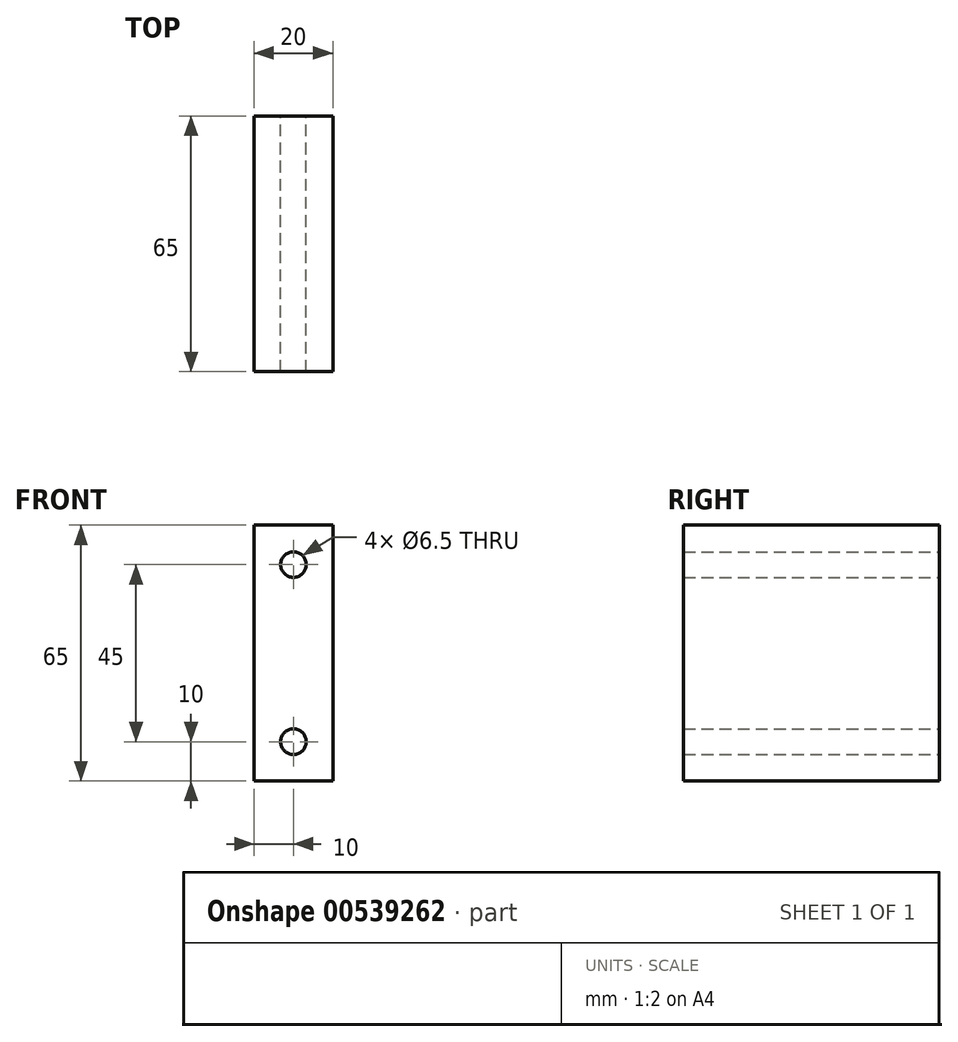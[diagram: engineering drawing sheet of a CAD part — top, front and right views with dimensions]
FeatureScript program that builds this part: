
annotation { "Feature Type Name" : "Feature", "Feature Type Description" : "" }
export const myFeature = defineFeature(function(context is Context, id is Id, definition is map)
    precondition{}
    {
        {
            var Q0;
            Q0=qCreatedBy(makeId("Front.planeOp"),FACE);
            var sketch = newSketch(context, id + "F0", { "sketchPlane" : qUnion([Q0])});
            skLineSegment(sketch, "E0.bottom", {"start": v(0, 0) * mm, "end": v(20, 0) * mm});
            skLineSegment(sketch, "E0.top", {"start": v(0, 65) * mm, "end": v(20, 65) * mm});
            skLineSegment(sketch, "E0.left", {"start": v(0, 0) * mm, "end": v(0, 65) * mm});
            skLineSegment(sketch, "E0.right", {"start": v(20, 0) * mm, "end": v(20, 65) * mm});
            skLineSegment(sketch, "E1", {"start": v(0, 10) * mm, "end": v(10, 10) * mm});
            skLineSegment(sketch, "E2", {"start": v(0, 55) * mm, "end": v(10, 55) * mm});
            skCircle(sketch, "E3", {"center": v(10, 55) * mm, "radius": 3.25 * mm});
            skCircle(sketch, "E4", {"center": v(10, 10) * mm, "radius": 3.25 * mm});
            skSolve(sketch);
        }
        {
            var Q0;
            Q0=makeQuery(id+"F0.imprint","IMPRINT",FACE,{"disambiguationData":[TD([[makeQuery(id+"F0.imprint","IMPRINT",EDGE,{"derivedFrom":sQuery(id+"F0.wireOp",EDGE,"E3")}),-1.0]])]});
            var Q1;
            Q1=makeQuery(id+"F0.imprint","IMPRINT",FACE,{"disambiguationData":[TD([[makeQuery(id+"F0.imprint","IMPRINT",EDGE,{"derivedFrom":sQuery(id+"F0.wireOp",EDGE,"94dded7e-ffbe-4f53-a43a-50ec608be8390.MirrorC")}),1.0]])]});
            var Q2;
            Q2=makeQuery(id+"F0.imprint","IMPRINT",FACE,{"disambiguationData":[TD([[makeQuery(id+"F0.imprint","IMPRINT",EDGE,{"derivedFrom":sQuery(id+"F0.wireOp",EDGE,"725528f7-230d-490f-96c3-0352711715200.MirrorC")}),1.0]])]});
            var Q3;
            {var subQ5=sQuery(id+"F0.wireOp",EDGE,"NzWXYV9I-SoYN-Hgyj-b80R-Zs6ElDGVtiVE");Q3=makeQuery(id+"F0.imprint","IMPRINT",FACE,{"disambiguationData":[TD([[makeQuery(id+"F0.imprint","IMPRINT",EDGE,{"derivedFrom":subQ5}),-1.0]])]});}
            var Q4;
            Q4=makeQuery(id+"F0.imprint","IMPRINT",FACE,{"disambiguationData":[TD([[makeQuery(id+"F0.imprint","IMPRINT",EDGE,{"derivedFrom":sQuery(id+"F0.wireOp",EDGE,"E4")}),-1.0]])]});
            extrude(context, id + "F1", {"entities" : qUnion([Q0, Q1, Q2, Q3, Q4]), "depth" : 65 * mm, "offsetDistance" : 25 * mm});
        }
    });
